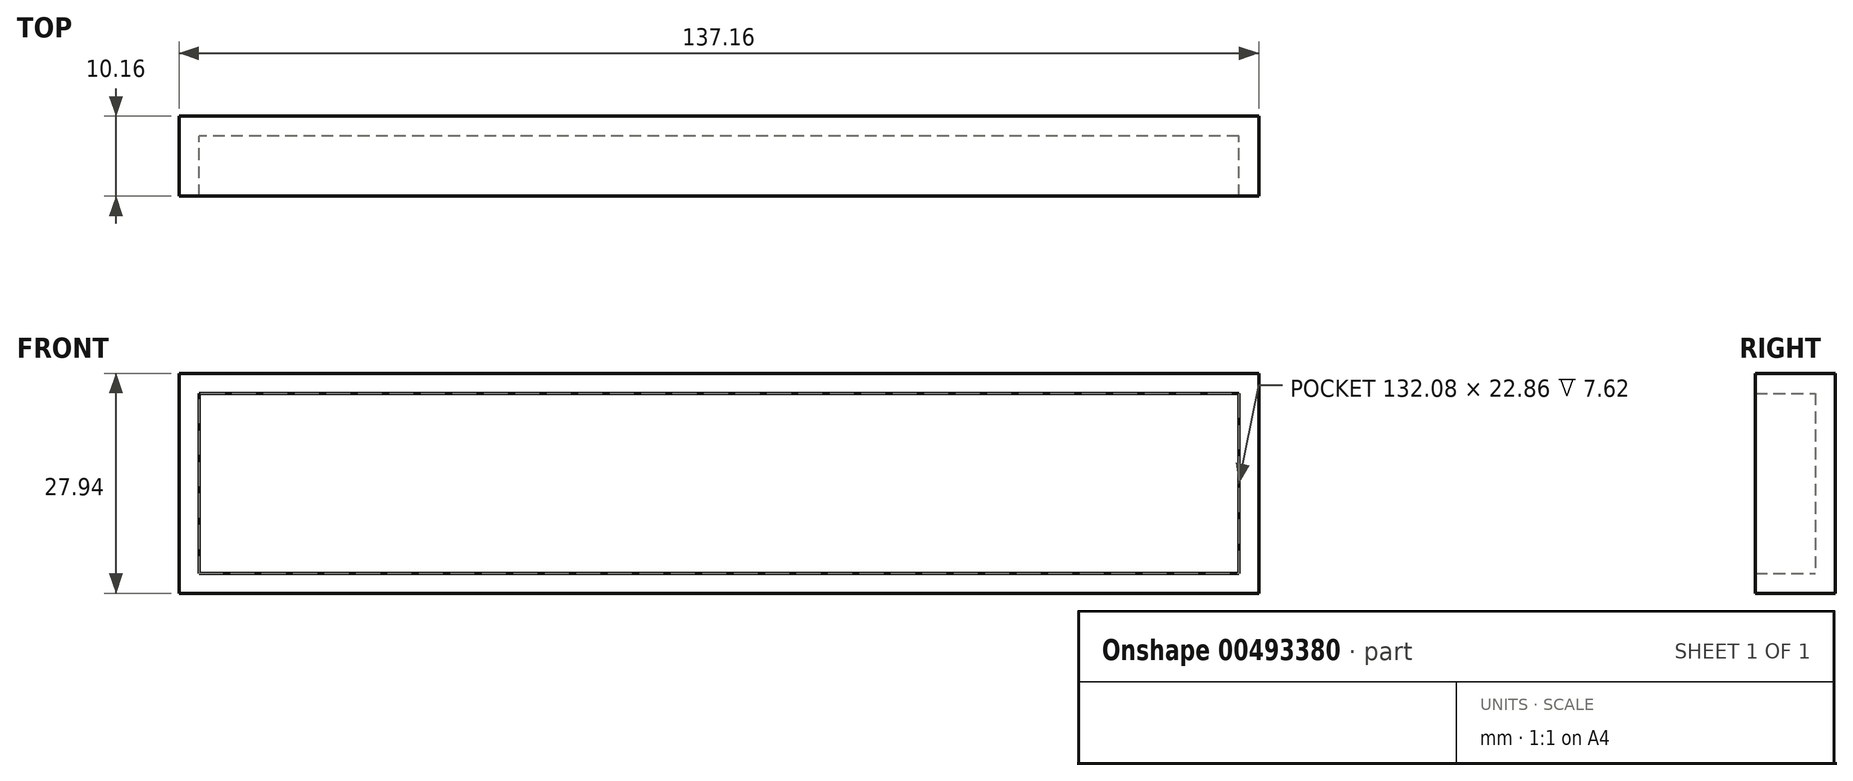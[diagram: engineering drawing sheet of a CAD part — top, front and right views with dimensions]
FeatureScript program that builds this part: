
annotation { "Feature Type Name" : "Feature", "Feature Type Description" : "" }
export const myFeature = defineFeature(function(context is Context, id is Id, definition is map)
    precondition{}
    {
        {
            var Q0;
            Q0=qCreatedBy(makeId("Front.planeOp"),FACE);
            var sketch = newSketch(context, id + "F0", { "sketchPlane" : qUnion([Q0])});
            skLineSegment(sketch, "E0.bottom", {"start": v(66.04, 11.43) * mm, "end": v(-66.04, 11.43) * mm});
            skLineSegment(sketch, "E0.top", {"start": v(66.04, -11.43) * mm, "end": v(-66.04, -11.43) * mm});
            skLineSegment(sketch, "E0.left", {"start": v(66.04, 11.43) * mm, "end": v(66.04, -11.43) * mm});
            skLineSegment(sketch, "E0.right", {"start": v(-66.04, 11.43) * mm, "end": v(-66.04, -11.43) * mm});
            skPoint(sketch, "E0.middle", {"position": v(0, 0) * mm});
            skSolve(sketch);
        }
        {
            var Q0;
            Q0=makeQuery(id+"F0.imprint","IMPRINT",FACE,{"disambiguationData":[TD([[makeQuery(id+"F0.imprint","IMPRINT",EDGE,{"derivedFrom":sQuery(id+"F0.wireOp",EDGE,"E0.bottom")}),1.0]])]});
            extrude(context, id + "F1", {"entities" : qUnion([Q0]), "endBound" : BoundingType.SYMMETRIC, "depth" : 7.62 * mm});
        }
        {
            var Q0;
            Q0=makeQuery(id+"F1.opExtrude","CAP_FACE",FACE,{"disambiguationData":[OSD([sQuery(id+"F0.wireOp",EDGE,"E0.bottom"),sQuery(id+"F0.wireOp",EDGE,"E0.top"),sQuery(id+"F0.wireOp",EDGE,"E0.left"),sQuery(id+"F0.wireOp",EDGE,"E0.right")])],"isStart":false});
            shell(context, id + "F2", {"entities" : qUnion([Q0]), "thickness" : 2.54 * mm, "oppositeDirection" : true});
        }
    });
